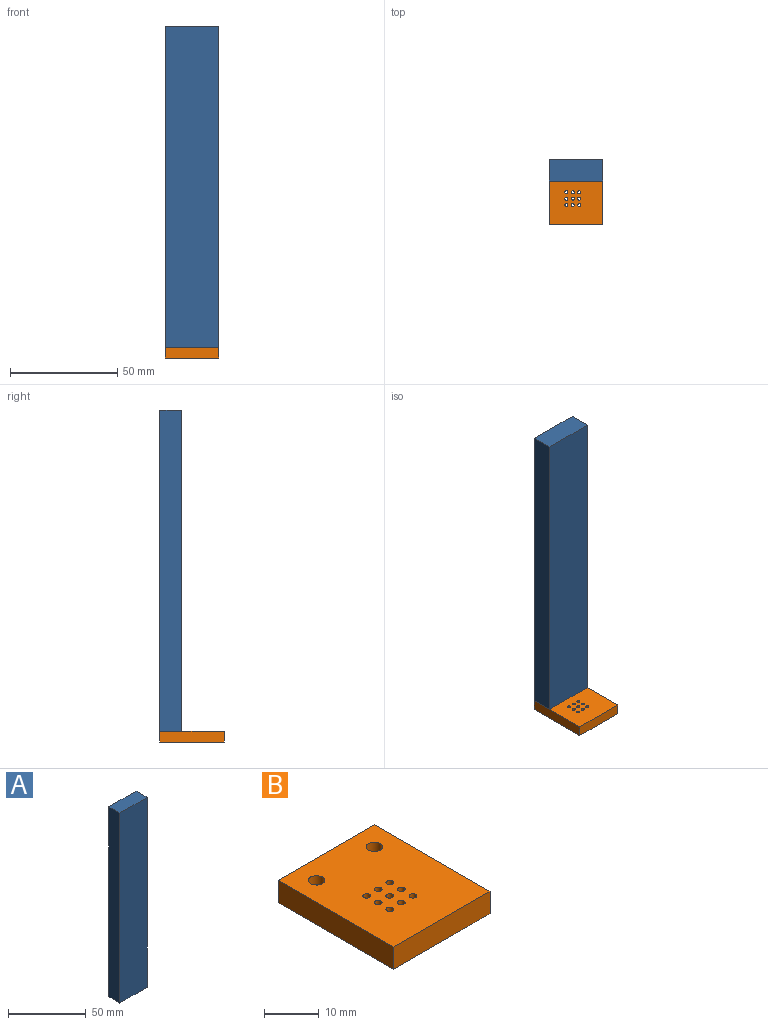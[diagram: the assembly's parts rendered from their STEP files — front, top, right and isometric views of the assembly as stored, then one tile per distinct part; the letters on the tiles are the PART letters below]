
ASSEMBLY  parts=2 mates=1
PART A: 10 faces, bbox 25x10x150 mm
  f0: plane 150x25mm, normal (0,1,0), area 3750mm2, adj f1,f3,f4,f5
  f1: plane 150x10mm, normal (-1,0,0), area 1500mm2, adj f0,f2,f4,f5
  f2: plane 150x25mm, normal (0,-1,0), area 3750mm2, adj f1,f3,f4,f5
  f3: plane 150x10mm, normal (1,0,0), area 1500mm2, adj f0,f2,f4,f5
  f4: plane 25x10mm, normal (0,0,1), area 250mm2, adj f0,f1,f2,f3
  f5: plane 25x10mm, normal (0,0,-1), area 235.9mm2, adj f0,f1,f2,f3,f6,f8
  f6: cylinder r=1.5mm len=20mm, axis (0,0,-1), area 188.5mm2, adj f5,f7
  f7: plane 3x3mm, normal (0,0,-1), area 7.1mm2, adj f6
  f8: cylinder r=1.5mm len=20mm, axis (0,0,-1), area 188.5mm2, adj f5,f9
  f9: plane 3x3mm, normal (0,0,-1), area 7.1mm2, adj f8
PART B: 21 faces, bbox 25x30x5 mm
  f0: plane 30x5mm, normal (-1,0,0), area 150mm2, adj f1,f3,f4,f5
  f1: plane 25x5mm, normal (0,-1,0), area 125mm2, adj f0,f2,f4,f5
  f2: plane 30x5mm, normal (1,0,0), area 150mm2, adj f1,f3,f4,f5
  f3: plane 25x5mm, normal (0,1,0), area 125mm2, adj f0,f2,f4,f5
  f4: plane 30x25mm, normal (0,0,1), area 722mm2, adj f0,f1,f2,f3,f6,f9,f12,f13
  f5: plane 30x25mm, normal (0,0,-1), area 696.9mm2, adj f0,f1,f2,f3,f8,f11,f12,f13
  f6: cylinder r=1.5mm len=3mm, axis (0,0,-1), area 18.8mm2, adj f4,f7
  f7: plane 5x5mm, normal (0,0,-1), area 12.6mm2, adj f6,f8
  f8: cylinder r=2.5mm len=5mm, axis (0,0,-1), area 47.1mm2, adj f5,f7
  f9: cylinder r=1.5mm len=3mm, axis (0,0,-1), area 18.8mm2, adj f4,f10
  f10: plane 5x5mm, normal (0,0,-1), area 12.6mm2, adj f9,f11
  f11: cylinder r=2.5mm len=5mm, axis (0,0,-1), area 47.1mm2, adj f5,f10
  f12: cylinder r=0.7mm len=5mm, axis (0,0,1), area 22mm2, adj f4,f5
  f13: cylinder r=0.7mm len=5mm, axis (0,0,1), area 22mm2, adj f4,f5
  f14: cylinder r=0.7mm len=5mm, axis (0,0,1), area 22mm2, adj f4,f5
  f15: cylinder r=0.7mm len=5mm, axis (0,0,1), area 22mm2, adj f4,f5
  f16: cylinder r=0.7mm len=5mm, axis (0,0,1), area 22mm2, adj f4,f5
  f17: cylinder r=0.7mm len=5mm, axis (0,0,1), area 22mm2, adj f4,f5
  f18: cylinder r=0.7mm len=5mm, axis (0,0,1), area 22mm2, adj f4,f5
  f19: cylinder r=0.7mm len=5mm, axis (0,0,1), area 22mm2, adj f4,f5
  f20: cylinder r=0.7mm len=5mm, axis (0,0,1), area 22mm2, adj f4,f5
PLACE A t=(-33.03,-10.05,13.54)mm
PLACE B t=(-33.03,-40.05,8.54)mm
MATE fastened B.f6 <-> A.f8  axis (0,0,1) through (-28.03,-15.05,13.54)mm
